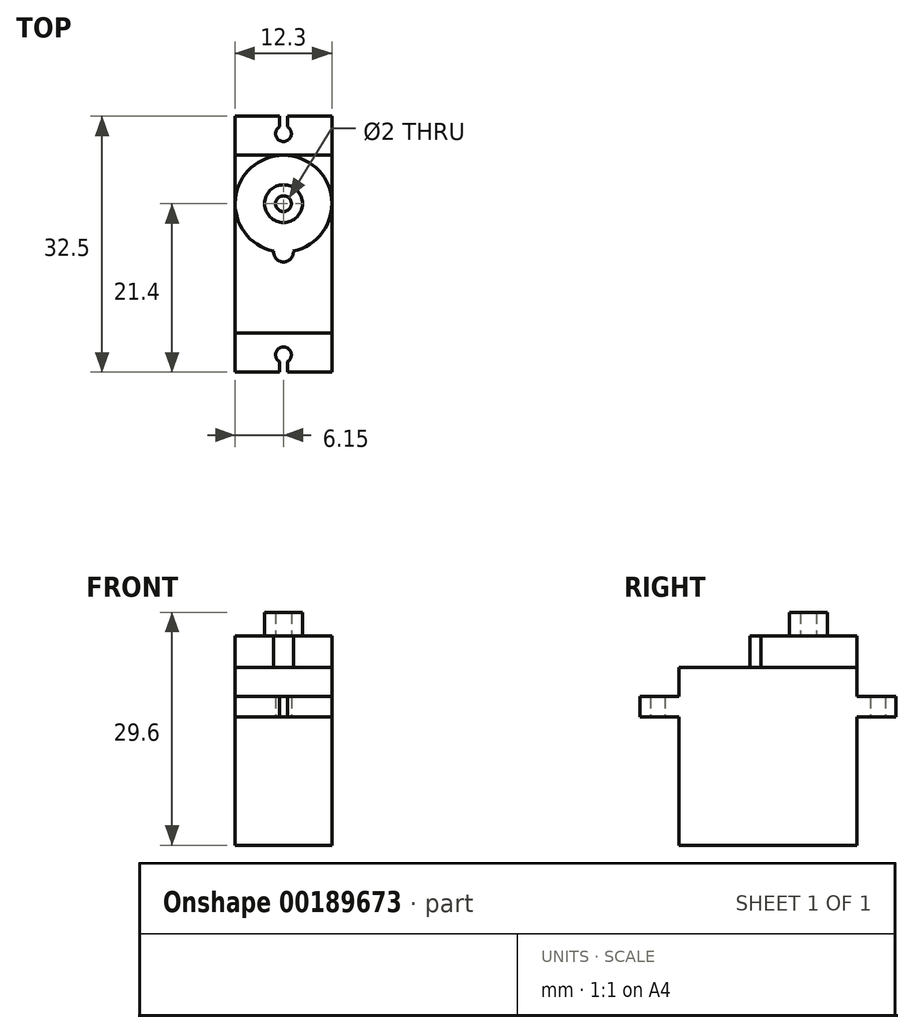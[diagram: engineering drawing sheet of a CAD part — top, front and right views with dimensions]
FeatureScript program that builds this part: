
annotation { "Feature Type Name" : "Feature", "Feature Type Description" : "" }
export const myFeature = defineFeature(function(context is Context, id is Id, definition is map)
    precondition{}
    {
        {
            var Q0;
            Q0=qCreatedBy(makeId("Top.planeOp"),FACE);
            var sketch = newSketch(context, id + "F0", { "sketchPlane" : qUnion([Q0])});
            skLineSegment(sketch, "E0.bottom", {"start": v(6.15, 11.3) * mm, "end": v(-6.15, 11.3) * mm});
            skLineSegment(sketch, "E0.top", {"start": v(6.15, -11.3) * mm, "end": v(-6.15, -11.3) * mm});
            skLineSegment(sketch, "E0.left", {"start": v(6.15, 11.3) * mm, "end": v(6.15, -11.3) * mm});
            skLineSegment(sketch, "E0.right", {"start": v(-6.15, 11.3) * mm, "end": v(-6.15, -11.3) * mm});
            skPoint(sketch, "E0.middle", {"position": v(0, 0) * mm});
            skSolve(sketch);
        }
        {
            var Q0;
            Q0=makeQuery(id+"F0.imprint","IMPRINT",FACE,{"disambiguationData":[TD([[makeQuery(id+"F0.imprint","IMPRINT",EDGE,{"derivedFrom":sQuery(id+"F0.wireOp",EDGE,"E0.bottom")}),1.0]])]});
            extrude(context, id + "F1", {"entities" : qUnion([Q0]), "depth" : 16.3 * mm});
        }
        {
            var Q0;
            Q0=makeQuery(id+"F1.opExtrude","CAP_FACE",FACE,{"disambiguationData":[OSD([sQuery(id+"F0.wireOp",EDGE,"E0.bottom"),sQuery(id+"F0.wireOp",EDGE,"E0.top"),sQuery(id+"F0.wireOp",EDGE,"E0.left"),sQuery(id+"F0.wireOp",EDGE,"E0.right")])],"isStart":false});
            var sketch = newSketch(context, id + "F2", { "sketchPlane" : qUnion([Q0])});
            skLineSegment(sketch, "E1.0", {"start": v(-6.15, 11.3) * mm, "end": v(-6.15, -11.3) * mm});
            skLineSegment(sketch, "E2.0", {"start": v(6.15, 11.3) * mm, "end": v(6.15, -11.3) * mm});
            skLineSegment(sketch, "E3", {"start": v(-6.15, 11.3) * mm, "end": v(-6.15, 16.25) * mm});
            skLineSegment(sketch, "E4", {"start": v(-6.15, 16.25) * mm, "end": v(6.15, 16.25) * mm});
            skLineSegment(sketch, "E5", {"start": v(6.15, 16.25) * mm, "end": v(6.15, 11.3) * mm});
            skLineSegment(sketch, "E6", {"start": v(0, 16.25) * mm, "end": v(0, 14.05) * mm, "construction": true});
            skPoint(sketch, "E6.endSnap0", {"position": v(0, 16.25) * mm});
            skCircle(sketch, "E7", {"center": v(0, 14.05) * mm, "radius": 1 * mm});
            skLineSegment(sketch, "E8", {"start": v(0.5, 14.92) * mm, "end": v(0.5, 16.25) * mm});
            skLineSegment(sketch, "E9.MirrorCS", {"start": v(-0.5, 14.92) * mm, "end": v(-0.5, 16.25) * mm});
            skLineSegment(sketch, "E10", {"start": v(0, 0) * mm, "end": v(2.74, 0) * mm, "construction": true});
            skLineSegment(sketch, "E11.MirrorCS", {"start": v(-6.15, -11.3) * mm, "end": v(-6.15, -16.25) * mm});
            skLineSegment(sketch, "E12.MirrorCS", {"start": v(-6.15, -16.25) * mm, "end": v(6.15, -16.25) * mm});
            skLineSegment(sketch, "E13.MirrorCS", {"start": v(6.15, -16.25) * mm, "end": v(6.15, -11.3) * mm});
            skCircle(sketch, "E14.MirrorC", {"center": v(0, -14.05) * mm, "radius": 1 * mm});
            skLineSegment(sketch, "E15.MirrorCS", {"start": v(-0.5, -14.92) * mm, "end": v(-0.5, -16.25) * mm});
            skLineSegment(sketch, "E16.MirrorCS", {"start": v(0.5, -14.92) * mm, "end": v(0.5, -16.25) * mm});
            skSolve(sketch);
        }
        {
            var Q0;
            {var subQ3=sQuery(id+"F2.wireOp",EDGE,"E3");Q0=makeQuery(id+"F2.imprint","IMPRINT",FACE,{"disambiguationData":[TD([[makeQuery(id+"F2.imprint","IMPRINT",EDGE,{"derivedFrom":subQ3}),-1.0]])]});}
            var Q1;
            Q1=makeQuery(id+"F2.imprint","IMPRINT",FACE,{"disambiguationData":[TD([[makeQuery(id+"F2.imprint","IMPRINT",EDGE,{"derivedFrom":sQuery(id+"F2.wireOp",EDGE,"E1.0")}),1.0]])]});
            var Q2;
            {var subQ5=sQuery(id+"F2.wireOp",EDGE,"E11.MirrorCS");Q2=makeQuery(id+"F2.imprint","IMPRINT",FACE,{"disambiguationData":[TD([[makeQuery(id+"F2.imprint","IMPRINT",EDGE,{"derivedFrom":subQ5}),1.0]])]});}
            extrude(context, id + "F3", {"entities" : qUnion([Q0, Q1, Q2]), "operationType" : NewBodyOperationType.ADD, "depth" : 2.6 * mm});
        }
        {
            var Q0;
            Q0=makeQuery(id+"F3.opExtrude","CAP_FACE",FACE,{"disambiguationData":[OSD([sQuery(id+"F2.wireOp",EDGE,"E1.0"),sQuery(id+"F2.wireOp",EDGE,"E2.0"),sQuery(id+"F2.wireOp",EDGE,"E3"),sQuery(id+"F2.wireOp",EDGE,"E4"),sQuery(id+"F2.wireOp",EDGE,"E5"),sQuery(id+"F2.wireOp",EDGE,"E7"),sQuery(id+"F2.wireOp",EDGE,"E8"),sQuery(id+"F2.wireOp",EDGE,"E9.MirrorCS"),sQuery(id+"F2.wireOp",EDGE,"E11.MirrorCS"),sQuery(id+"F2.wireOp",EDGE,"E12.MirrorCS"),sQuery(id+"F2.wireOp",EDGE,"E13.MirrorCS"),sQuery(id+"F2.wireOp",EDGE,"E14.MirrorC"),sQuery(id+"F2.wireOp",EDGE,"E15.MirrorCS"),sQuery(id+"F2.wireOp",EDGE,"E16.MirrorCS")])],"isStart":false});
            var sketch = newSketch(context, id + "F4", { "sketchPlane" : qUnion([Q0])});
            skLineSegment(sketch, "E17.0", {"start": v(6.15, -11.3) * mm, "end": v(-6.15, -11.3) * mm});
            skLineSegment(sketch, "E18.0", {"start": v(6.15, 11.3) * mm, "end": v(-6.15, 11.3) * mm});
            skLineSegment(sketch, "E19", {"start": v(6.15, 11.3) * mm, "end": v(6.15, -11.3) * mm});
            skLineSegment(sketch, "E20", {"start": v(-6.15, 11.3) * mm, "end": v(-6.15, -11.3) * mm});
            skSolve(sketch);
        }
        {
            var Q0;
            Q0=makeQuery(id+"F4.imprint","IMPRINT",FACE,{"disambiguationData":[TD([[makeQuery(id+"F4.imprint","IMPRINT",EDGE,{"derivedFrom":sQuery(id+"F4.wireOp",EDGE,"E17.0")}),-1.0]])]});
            extrude(context, id + "F5", {"entities" : qUnion([Q0]), "operationType" : NewBodyOperationType.ADD, "depth" : 3.7 * mm});
        }
        {
            var Q0;
            Q0=makeQuery(id+"F5.opExtrude","CAP_FACE",FACE,{"disambiguationData":[OSD([sQuery(id+"F4.wireOp",EDGE,"E17.0"),sQuery(id+"F4.wireOp",EDGE,"E18.0"),sQuery(id+"F4.wireOp",EDGE,"E19"),sQuery(id+"F4.wireOp",EDGE,"E20")])],"isStart":false});
            var sketch = newSketch(context, id + "F6", { "sketchPlane" : qUnion([Q0])});
            skCircle(sketch, "E21", {"center": v(0, 5.15) * mm, "radius": 6.15 * mm});
            skLineSegment(sketch, "E22.0", {"start": v(6.15, 11.3) * mm, "end": v(6.15, -11.3) * mm, "construction": true});
            skLineSegment(sketch, "E23.0", {"start": v(6.15, 11.3) * mm, "end": v(-6.15, 11.3) * mm, "construction": true});
            skCircle(sketch, "E24", {"center": v(0, -1) * mm, "radius": 1.25 * mm});
            skSolve(sketch);
        }
        {
            var Q0;
            {var subQ1=sQuery(id+"F6.wireOp",EDGE,"E21");var subQ4=makeQuery(id+"F6.imprint","INTERSECT",VERTEX,{"derivedFrom":[makeQuery(id+"F5.opExtrude","CAP_EDGE",EDGE,{"disambiguationData":[OSD([sQuery(id+"F4.wireOp",EDGE,"E18.0")])],"isStart":false}),subQ1]});Q0=makeQuery(id+"F6.imprint","IMPRINT",FACE,{"disambiguationData":[TD([[makeQuery(id+"F6.imprint","IMPRINT",EDGE,{"disambiguationData":[TD([[subQ4,1.0]])],"derivedFrom":subQ1}),1.0]])]});}
            var Q1;
            {var subQ0=sQuery(id+"F6.wireOp",EDGE,"E24");var subQ1=sQuery(id+"F6.wireOp",EDGE,"E21");var subQ2=makeQuery(id+"F6.imprint","INTERSECT",VERTEX,{"disambiguationData":[OD(0.0)],"derivedFrom":[subQ1,subQ0]});Q1=makeQuery(id+"F6.imprint","IMPRINT",FACE,{"disambiguationData":[TD([[makeQuery(id+"F6.imprint","IMPRINT",EDGE,{"disambiguationData":[TD([[subQ2,-1.0]])],"derivedFrom":subQ1}),-1.0]])]});}
            var Q2;
            {var subQ0=sQuery(id+"F6.wireOp",EDGE,"E24");var subQ1=sQuery(id+"F6.wireOp",EDGE,"E21");var subQ2=makeQuery(id+"F6.imprint","INTERSECT",VERTEX,{"disambiguationData":[OD(0.0)],"derivedFrom":[subQ1,subQ0]});Q2=makeQuery(id+"F6.imprint","IMPRINT",FACE,{"disambiguationData":[TD([[makeQuery(id+"F6.imprint","IMPRINT",EDGE,{"disambiguationData":[TD([[subQ2,-1.0]])],"derivedFrom":subQ1}),1.0]])]});}
            extrude(context, id + "F7", {"entities" : qUnion([Q0, Q1, Q2]), "operationType" : NewBodyOperationType.ADD, "depth" : 4 * mm});
        }
        {
            var Q0;
            Q0=makeQuery(id+"F7.opExtrude","CAP_FACE",FACE,{"disambiguationData":[OSD([sQuery(id+"F6.wireOp",EDGE,"E21"),sQuery(id+"F6.wireOp",EDGE,"E24")])],"isStart":false});
            var sketch = newSketch(context, id + "F8", { "sketchPlane" : qUnion([Q0])});
            skArc(sketch, "E25.0", {"start": v(1.24, -0.87) * mm, "mid": v(0, 11.3) * mm, "end": v(-1.24, -0.87) * mm, "construction": true});
            skCircle(sketch, "E26", {"center": v(0, 5.15) * mm, "radius": 2.4 * mm});
            skCircle(sketch, "E27", {"center": v(0, 5.15) * mm, "radius": 1 * mm});
            skSolve(sketch);
        }
        {
            var Q0;
            Q0=makeQuery(id+"F8.imprint","IMPRINT",FACE,{"disambiguationData":[TD([[makeQuery(id+"F8.imprint","IMPRINT",EDGE,{"derivedFrom":sQuery(id+"F8.wireOp",EDGE,"E26")}),1.0]])]});
            extrude(context, id + "F9", {"entities" : qUnion([Q0]), "depth" : 3 * mm});
        }
    });
